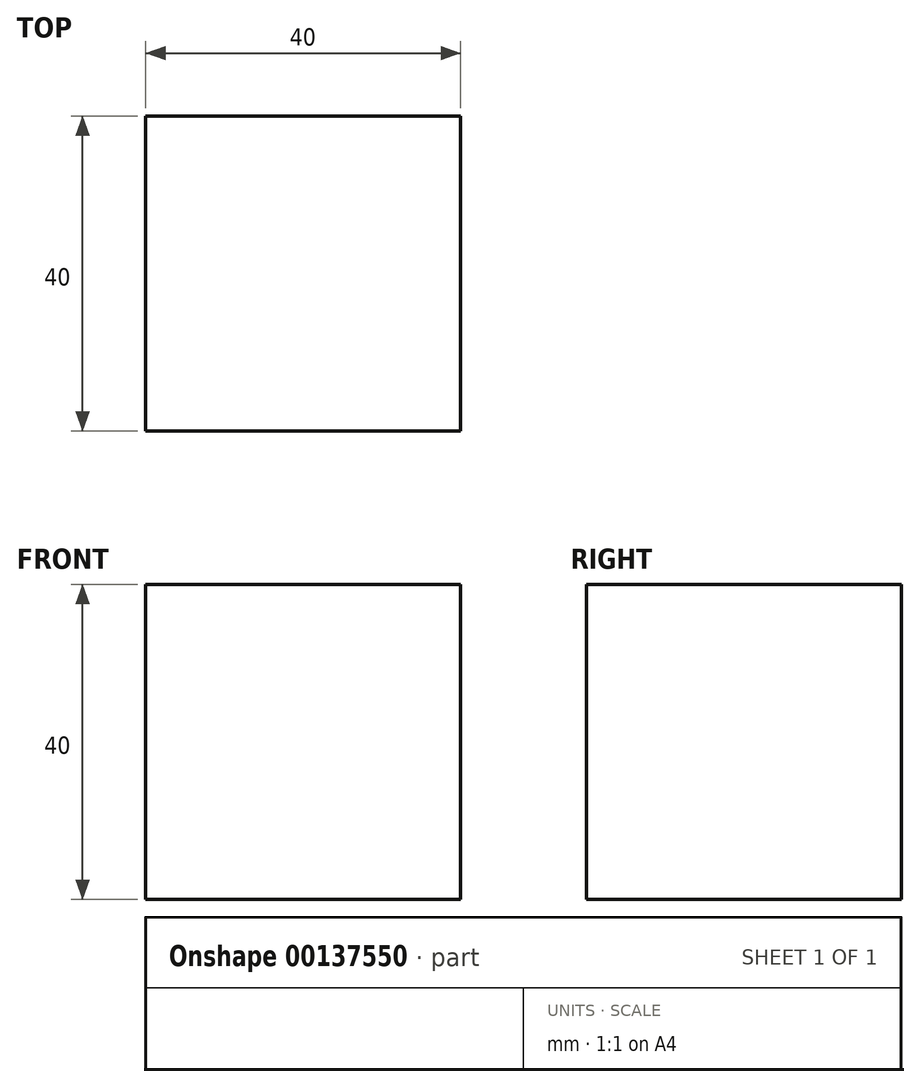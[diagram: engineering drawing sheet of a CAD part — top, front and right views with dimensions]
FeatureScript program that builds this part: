
annotation { "Feature Type Name" : "Feature", "Feature Type Description" : "" }
export const myFeature = defineFeature(function(context is Context, id is Id, definition is map)
    precondition{}
    {
        {
            var Q0;
            Q0=qCreatedBy(makeId("Top.planeOp"),FACE);
            var sketch = newSketch(context, id + "F0", { "sketchPlane" : qUnion([Q0])});
            skLineSegment(sketch, "E0.bottom", {"start": v(-3.54, 5.27) * mm, "end": v(36.46, 5.27) * mm});
            skLineSegment(sketch, "E0.top", {"start": v(-3.54, -34.73) * mm, "end": v(36.46, -34.73) * mm});
            skLineSegment(sketch, "E0.left", {"start": v(-3.54, 5.27) * mm, "end": v(-3.54, -34.73) * mm});
            skLineSegment(sketch, "E0.right", {"start": v(36.46, 5.27) * mm, "end": v(36.46, -34.73) * mm});
            skSolve(sketch);
        }
        {
            var Q0;
            Q0=makeQuery(id+"F0.imprint","IMPRINT",FACE,{"disambiguationData":[TD([[makeQuery(id+"F0.imprint","IMPRINT",EDGE,{"derivedFrom":sQuery(id+"F0.wireOp",EDGE,"E0.bottom")}),-1.0]])]});
            extrude(context, id + "F1", {"entities" : qUnion([Q0]), "depth" : 40 * mm});
        }
    });
